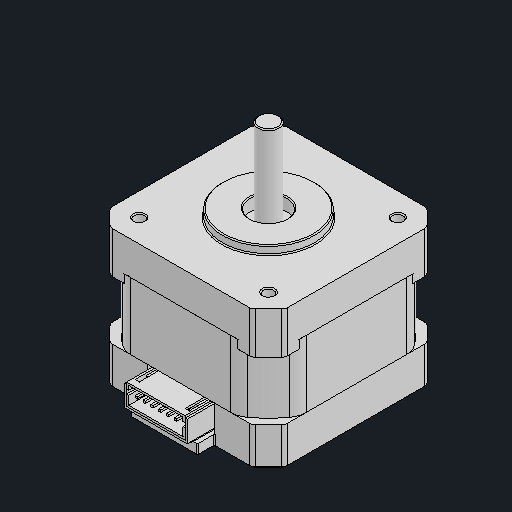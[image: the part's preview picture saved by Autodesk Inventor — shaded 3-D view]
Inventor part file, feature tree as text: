
AUTODESK INVENTOR PART (.ipt)
format: ipt  version: 2024.2 (Build 282272000, 272)  size: 435,712 bytes
history: native  units: mm
features: other x7, fillet x2, extrude x1
ambient origin geometry x8: Origin, YZ Plane, XZ Plane, XY Plane, X Axis, Y Axis, Z Axis, Center Point
bodies: Body1 (feature_tree), Body2 (feature_tree), Body3 (feature_tree), Body4 (feature_tree), Body5 (feature_tree)
feature tree (10):
  other  "솔리드1"
  other  "솔리드2"
  other  "솔리드3"
  other  "솔리드4"
  other  "솔리드5"
  fillet  "Fillet6"  [1 undecoded]
  other  "M3x0.5 Tapped Hole1"
  fillet  "Fillet11"  [1 undecoded]
  extrude  "Extrude-Thin1"  [1 undecoded]
  other  "Boss-Extrude14"
note: 3 required parameter values undecoded (feature->parameter linkage not recoverable at this tier; creation-order binding heuristic only, values carry confidence <= 0.55)
